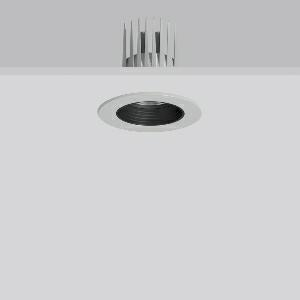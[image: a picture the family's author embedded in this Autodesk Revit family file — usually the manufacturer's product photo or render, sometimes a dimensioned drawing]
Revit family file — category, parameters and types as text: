
# Revit family: heledon_mini_e_901754_004_3_76_cace
name_source: partatom
category: Lighting Fixtures
units: mm (PartAtom-declared; Revit-internal decimal feet)

## family parameters
Cut with Voids When Loaded = No
Host = Face
Light Source = No
Part Type = Normal
Room Calculation Point = No
Round Connector Dimension = Use Diameter
Shared = No

## types (1)
- HELEDON mini E (1 x LED Modul 935, 3300 lm, 3500)
    Apparent Load = 29 VA
    Approval mark = CE
    CIE Flux Codes = 80 99 100 100 100
    Color Rendering = 92
    Color Temperature = 3500
    Default Elevation = 1800 mm
    Description = Series: HELEDON mini
Round recessed downlight. Housing: die-cast aluminium, powder-coated. Black plastic ring and recessed LED to prevent glare from the side. Optical assembly with lens made of plastic (polycarbonate) for the best homogeneous light distribution - can be changed without tools. Best colour rendering index Ra>90. Suitable for Recessed ceiling mounting. Installation without tools thanks to spring fastening system. Including separate LED converter with connecting cable 600 mm.High quality converter without flickering and stroboscopic effect. Through-wiring box (5 pole) available as accessory. The following accessories can be mounted without use of tools: interchangeable lenses, decorative glasses, honeycomb louvre, clear and frosted diffusers, white interchangeable plastic ring. 
Colour: silver
Diameter: 124 mm
Height: 3 mm
Cut-out diameter: 114 mm
Recess height: 170 mm
Luminaire: recess height: 120 mm
Lamp: LED
Socket: without socket
Colour temperature: 3500K
Colour rendering index (CRI): 92
System power: 29 W
Rated luminous flux: 3300 lm
Luminous efficiency: 114 lm/W
Control gear: Converter, dimmable, DALI
Protection class: II
Type of protection: IP 20
    Height = 0 mm  [stored 0 ft]
    Lamp = 1 x LED Modul 935
    Lamp Light Flux = 3300 lm
    Lamp count = 1
    Length = 124 mm  [stored 0.406824 ft]
    Lifetime = 50000 h
    Luminous efficacy = 114 lm/W
    Manufacturer = RZB
    ModVariant = No
    Model = 901754.004.3.76
    Mounting Place = Ceiling
    Mounting Type = Recessed
    Number of Poles = 1
    OnlyDefault = Yes
    Power Factor = 1
    Product Name = HELEDON mini E
    Product group = Recessed downlights
    ProductGroupID = 402
    Protection Class = Protection class II
    Protection Degree = IP 20
    RLX_Detail_Level = 1
    RLX_Emergency_Light_Flux = 0 lm
    RLX_Emergency_Type = 0
    RLX_Emergency_Type_DB = No
    RlxData = <blob elided: 126109 chars, md5=28a69410>
    Socket = socket
    Standby Power = 0 W
    System Light Flux = 3300 lm
    System Power = 29 W
    Type Comments = Product without accessories
    Type Image = 901656.004.jpg
    URL = http://relux.com
    VarID = ---
    Voltage = 230 V
    Voltage Range = 220-240 V
    Weight = 0.00 kg
    Width = 0 mm  [stored 0 ft]

note: [stored X ft] marks values corroborated as IEEE doubles in the binary element streams (Revit-internal decimal feet)

## geometry (parser evidence)
native form markers: Blend x4, Sweep x12
no freeform markers — native parametric forms only
